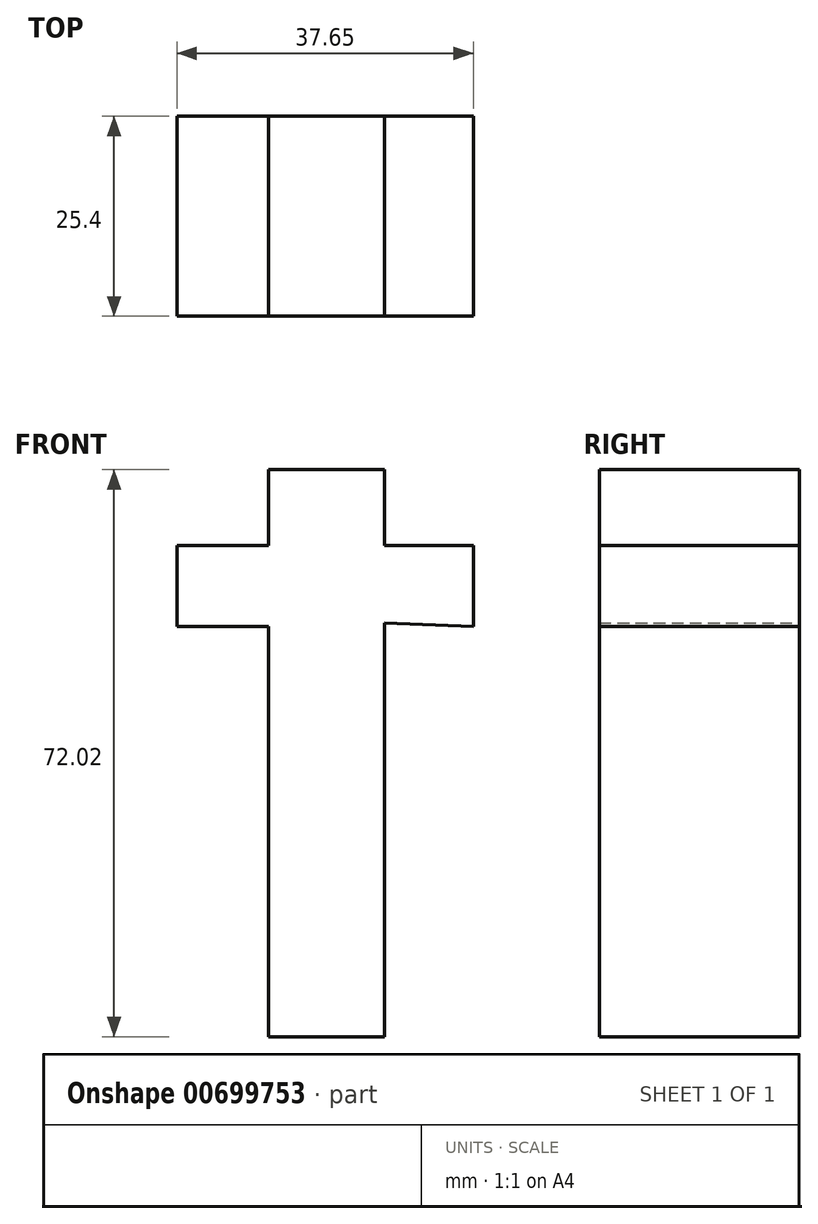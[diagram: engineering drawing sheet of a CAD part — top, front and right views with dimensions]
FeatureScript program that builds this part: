
annotation { "Feature Type Name" : "Feature", "Feature Type Description" : "" }
export const myFeature = defineFeature(function(context is Context, id is Id, definition is map)
    precondition{}
    {
        {
            var Q0;
            Q0=qCreatedBy(makeId("Front.planeOp"),FACE);
            var sketch = newSketch(context, id + "F0", { "sketchPlane" : qUnion([Q0])});
            skLineSegment(sketch, "E0", {"start": v(109.07, 31.01) * mm, "end": v(109.07, -21.56) * mm});
            skLineSegment(sketch, "E1", {"start": v(109.07, -21.56) * mm, "end": v(94.34, -21.56) * mm});
            skLineSegment(sketch, "E2", {"start": v(94.34, -21.56) * mm, "end": v(94.34, 30.55) * mm});
            skLineSegment(sketch, "E3", {"start": v(94.34, 30.55) * mm, "end": v(82.72, 30.55) * mm});
            skLineSegment(sketch, "E4", {"start": v(82.72, 30.55) * mm, "end": v(82.72, 40.83) * mm});
            skLineSegment(sketch, "E5", {"start": v(82.72, 40.83) * mm, "end": v(94.34, 40.83) * mm});
            skLineSegment(sketch, "E6", {"start": v(94.34, 40.83) * mm, "end": v(94.34, 50.46) * mm});
            skLineSegment(sketch, "E7", {"start": v(94.34, 50.46) * mm, "end": v(109.07, 50.46) * mm});
            skLineSegment(sketch, "E8", {"start": v(109.07, 50.46) * mm, "end": v(109.07, 40.83) * mm});
            skLineSegment(sketch, "E9", {"start": v(109.07, 40.83) * mm, "end": v(120.37, 40.83) * mm});
            skLineSegment(sketch, "E10", {"start": v(120.37, 41.07) * mm, "end": v(120.37, 30.55) * mm});
            skLineSegment(sketch, "E11", {"start": v(120.37, 30.55) * mm, "end": v(109.07, 31.01) * mm});
            skSolve(sketch);
        }
        {
            var Q0;
            Q0 = qSketchRegion(id + "F0", true);
            extrude(context, id + "F1", {"entities" : qUnion([Q0]), "depth" : 25.4 * mm, "offsetDistance" : 25.4 * mm});
        }
    });
